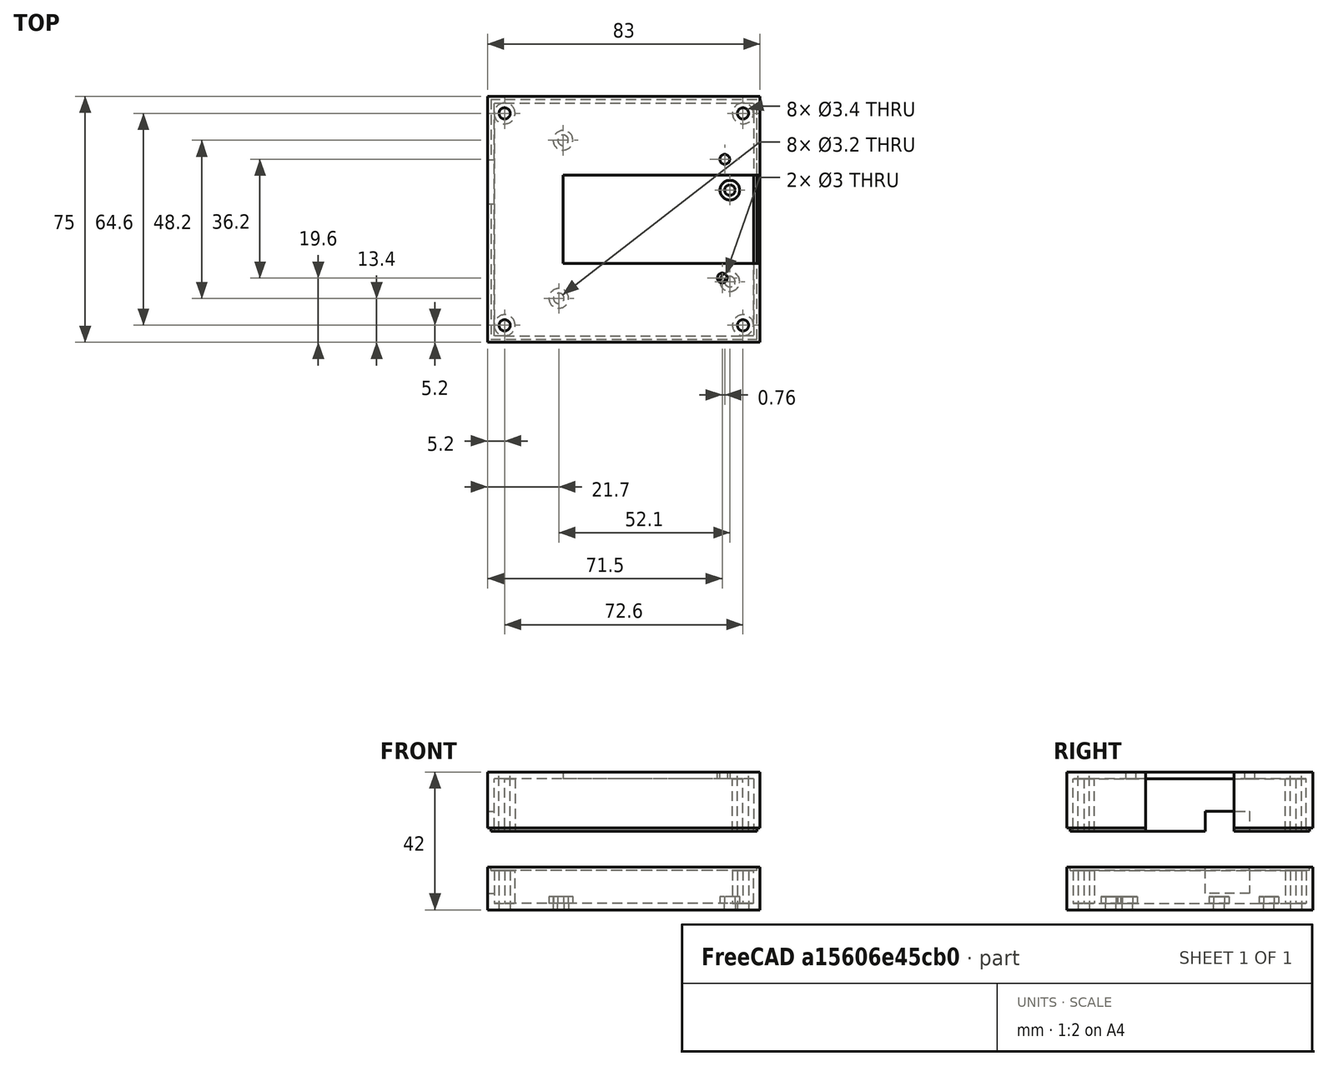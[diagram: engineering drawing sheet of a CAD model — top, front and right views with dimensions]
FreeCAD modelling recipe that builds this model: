
FCSTD DOCUMENT  (FreeCAD 0.19R23578 (Git))
Label: fond
License: All rights reserved
LicenseURL: http://en.wikipedia.org/wiki/All_rights_reserved
objects: Sketcher::SketchObject×15, PartDesign::Pad×9, PartDesign::Pocket×4, PartDesign::Hole×2, PartDesign::Body×2
note: 47 computed .brp shape members not serialized (recipe doc carries the construction recipe); baked Part::Feature solids carry a one-line shape summary decoded from their .brp

FEATURE [Sketcher::SketchObject] Sketch
  MapMode = 5
  Support = -> [XY_Plane]
  sketch-geometry (4):
    g0: LineSegment StartX=-41.5 StartY=37.5 StartZ=0 EndX=41.5 EndY=37.5 EndZ=0
    g1: LineSegment StartX=41.5 StartY=37.5 StartZ=0 EndX=41.5 EndY=-37.5 EndZ=0
    g2: LineSegment StartX=41.5 StartY=-37.5 StartZ=0 EndX=-41.5 EndY=-37.5 EndZ=0
    g3: LineSegment StartX=-41.5 StartY=-37.5 StartZ=0 EndX=-41.5 EndY=37.5 EndZ=0
  constraints (10):
    c: Coincident(g0,g1)
    c: Coincident(g1,g2)
    c: Coincident(g2,g3)
    c: Coincident(g3,g0)
    c: Horizontal(g2)
    c: Vertical(g1)
    c: DistanceX(g0,g0) = 83
    c: DistanceY(g3,g3) = 75
    c: Symmetric(g0,g0,g-2)
    c: Symmetric(g2,g0,g-1)
FEATURE [PartDesign::Pad] Pad  label="PlaqueFond"
  Direction = (1,1,1)
  Length = 2
  Length2 = 100
  Profile = -> Sketch
  Type = 0
FEATURE [Sketcher::SketchObject] Sketch001
  ExternalGeometry = -> [Pad]
  MapMode = 5
  Placement = pos=(0,0,2) rot=(0,0,1;0rad)
  Support = -> [Pad]
  sketch-geometry (9):
    g0: Circle CenterX=-18.5 CenterY=24.1 CenterZ=0 NormalX=0 NormalY=0 NormalZ=1 AngleXU=0 Radius=1.6
    g1: Circle CenterX=32.3 CenterY=8.9 CenterZ=0 NormalX=0 NormalY=0 NormalZ=1 AngleXU=0 Radius=1.6
    g2: Circle CenterX=32.3 CenterY=-19 CenterZ=0 NormalX=0 NormalY=0 NormalZ=1 AngleXU=0 Radius=1.6
    g3: Circle CenterX=-19.8 CenterY=-24.1 CenterZ=0 NormalX=0 NormalY=0 NormalZ=1 AngleXU=0 Radius=1.6
    g4: Circle CenterX=-19.8 CenterY=-24.1 CenterZ=0 NormalX=0 NormalY=0 NormalZ=1 AngleXU=0 Radius=3
    g5: Circle CenterX=32.3 CenterY=-19 CenterZ=0 NormalX=0 NormalY=0 NormalZ=1 AngleXU=0 Radius=3
    g6: Circle CenterX=32.3 CenterY=8.9 CenterZ=0 NormalX=0 NormalY=0 NormalZ=1 AngleXU=0 Radius=3
    g7: Circle CenterX=-18.5 CenterY=24.1 CenterZ=0 NormalX=0 NormalY=0 NormalZ=1 AngleXU=0 Radius=3
    g8: LineSegment StartX=-18.5 StartY=24.1 StartZ=0 EndX=-19.8 EndY=24.1 EndZ=0
  constraints (22):
    c: Vertical(g2,g1)
    c: DistanceY(g3,g2) = 5.1
    c: DistanceY(g2,g1) = 27.9
    c: DistanceY(g1,g0) = 15.2
    c: DistanceX(g3,g0) = 1.3
    c: DistanceX(g0,g1) = 50.8
    c: Radius(g3) = 1.6
    c: Equal(g3,g2)
    c: Equal(g3,g1)
    c: Equal(g3,g0)
    c: Coincident(g7,g0)
    c: Coincident(g4,g3)
    c: Coincident(g5,g2)
    c: Coincident(g6,g1)
    c: Radius(g5) = 3
    c: Equal(g5,g6)
    c: Equal(g5,g4)
    c: Equal(g5,g7)
    c: Coincident(g8,g0)
    c: Horizontal(g8)
    c: Symmetric(g8,g3,g-1)
    c: DistanceX(g-3,g0) = 23
FEATURE [PartDesign::Pad] Pad001  label="FixationArduino"
  BaseFeature = -> Pad
  Direction = (1,1,1)
  Length = 2
  Length2 = 100
  Profile = -> Sketch001
  Type = 0
FEATURE [Sketcher::SketchObject] Sketch002
  ExternalGeometry = -> [Pad001]
  MapMode = 5
  Placement = pos=(0,0,2) rot=(0,0,1;0rad)
  Support = -> [Pad001]
  sketch-geometry (8):
    g0: LineSegment StartX=-41.5 StartY=37.5 StartZ=0 EndX=41.5 EndY=37.5 EndZ=0
    g1: LineSegment StartX=41.5 StartY=37.5 StartZ=0 EndX=41.5 EndY=-37.5 EndZ=0
    g2: LineSegment StartX=41.5 StartY=-37.5 StartZ=0 EndX=-41.5 EndY=-37.5 EndZ=0
    g3: LineSegment StartX=-41.5 StartY=-37.5 StartZ=0 EndX=-41.5 EndY=37.5 EndZ=0
    g4: LineSegment StartX=-39.5 StartY=35.5 StartZ=0 EndX=39.5 EndY=35.5 EndZ=0
    g5: LineSegment StartX=39.5 StartY=35.5 StartZ=0 EndX=39.5 EndY=-35.5 EndZ=0
    g6: LineSegment StartX=39.5 StartY=-35.5 StartZ=0 EndX=-39.5 EndY=-35.5 EndZ=0
    g7: LineSegment StartX=-39.5 StartY=-35.5 StartZ=0 EndX=-39.5 EndY=35.5 EndZ=0
  constraints (20):
    c: Coincident(g0,g1)
    c: Coincident(g1,g2)
    c: Coincident(g2,g3)
    c: Coincident(g3,g0)
    c: Horizontal(g0)
    c: Horizontal(g2)
    c: Vertical(g1)
    c: Vertical(g3)
    c: Coincident(g4,g5)
    c: Coincident(g5,g6)
    c: Coincident(g6,g7)
    c: Coincident(g7,g4)
    c: Horizontal(g6)
    c: Vertical(g5)
    c: Coincident(g0,g-4)
    c: Coincident(g2,g-6)
    c: Symmetric(g4,g4,g-2)
    c: Symmetric(g6,g4,g-1)
    c: DistanceX(g0,g4) = 2
    c: DistanceY(g4,g0) = 2
FEATURE [PartDesign::Pad] Pad002  label="Rebord"
  BaseFeature = -> Pad001
  Direction = (1,1,1)
  Length = 10
  Length2 = 100
  Profile = -> Sketch002
  Type = 0
FEATURE [Sketcher::SketchObject] Sketch003
  ExternalGeometry = -> [Pad002]
  MapMode = 5
  Placement = pos=(-41.5,0,0) rot=(0.57735,-0.57735,-0.57735;2.0944rad)
  Support = -> [Pad002]
  sketch-geometry (4):
    g0: LineSegment StartX=-18.21 StartY=5 StartZ=0 EndX=-4.71 EndY=5 EndZ=0
    g1: LineSegment StartX=-4.71 StartY=5 StartZ=0 EndX=-4.71 EndY=12 EndZ=0
    g2: LineSegment StartX=-4.71 StartY=12 StartZ=0 EndX=-18.21 EndY=12 EndZ=0
    g3: LineSegment StartX=-18.21 StartY=12 StartZ=0 EndX=-18.21 EndY=5 EndZ=0
  constraints (12):
    c: Coincident(g0,g1)
    c: Coincident(g1,g2)
    c: Coincident(g2,g3)
    c: Coincident(g3,g0)
    c: Horizontal(g0)
    c: Horizontal(g2)
    c: Vertical(g1)
    c: Vertical(g3)
    c: PointOnObject(g2,g-3)
    c: DistanceX(g0,g0) = 13.5
    c: DistanceY(g-4,g0) = 3
    c: DistanceX(g1,g-1) = 4.71
FEATURE [PartDesign::Pocket] Pocket  label="OuvertureUSB"
  BaseFeature = -> Pad002
  Length = 0
  Length2 = 100
  Profile = -> Sketch003
  Type = 2
FEATURE [Sketcher::SketchObject] Sketch004
  ExternalGeometry = -> [Pocket]
  MapMode = 5
  Placement = pos=(0,0,2) rot=(0,0,1;0rad)
  Support = -> [Pocket]
  sketch-geometry (4):
    g0: Circle CenterX=32.3 CenterY=8.9 CenterZ=0 NormalX=0 NormalY=0 NormalZ=1 AngleXU=0 Radius=1.6
    g1: Circle CenterX=32.3 CenterY=-19 CenterZ=0 NormalX=0 NormalY=0 NormalZ=1 AngleXU=0 Radius=1.6
    g2: Circle CenterX=-19.8 CenterY=-24.1 CenterZ=0 NormalX=0 NormalY=0 NormalZ=1 AngleXU=0 Radius=1.6
    g3: Circle CenterX=-18.5 CenterY=24.1 CenterZ=0 NormalX=0 NormalY=0 NormalZ=1 AngleXU=0 Radius=1.6
  constraints (8):
    c: Coincident(g3,g-6)
    c: Coincident(g0,g-3)
    c: Coincident(g1,g-4)
    c: Coincident(g2,g-5)
    c: Radius(g2) = 1.6
    c: Equal(g2,g1)
    c: Equal(g2,g0)
    c: Equal(g2,g3)
FEATURE [PartDesign::Pocket] Pocket001  label="TrouFixationArduino"
  BaseFeature = -> Pocket
  Length = 5
  Length2 = 100
  Profile = -> Sketch004
  Type = 2
FEATURE [Sketcher::SketchObject] Sketch005
  ExternalGeometry = -> [Pocket001]
  MapMode = 5
  Placement = pos=(0,0,12) rot=(0,0,1;0rad)
  Support = -> [Pocket001]
  sketch-geometry (12):
    g0: LineSegment StartX=41.5 StartY=37.5 StartZ=0 EndX=-41.5 EndY=37.5 EndZ=0
    g1: LineSegment StartX=41.5 StartY=-37.5 StartZ=0 EndX=41.5 EndY=37.5 EndZ=0
    g2: LineSegment StartX=41.5 StartY=-37.5 StartZ=0 EndX=-41.5 EndY=-37.5 EndZ=0
    g3: LineSegment StartX=-40.5 StartY=-36.5 StartZ=0 EndX=-40.5 EndY=4.71 EndZ=0
    g4: LineSegment StartX=-40.5 StartY=4.71 StartZ=0 EndX=-41.5 EndY=4.71 EndZ=0
    g5: LineSegment StartX=-41.5 StartY=4.71 StartZ=0 EndX=-41.5 EndY=-37.5 EndZ=0
    g6: LineSegment StartX=-40.5 StartY=36.5 StartZ=0 EndX=-40.5 EndY=18.21 EndZ=0
    g7: LineSegment StartX=-40.5 StartY=18.21 StartZ=0 EndX=-41.5 EndY=18.21 EndZ=0
    g8: LineSegment StartX=-41.5 StartY=18.21 StartZ=0 EndX=-41.5 EndY=37.5 EndZ=0
    g9: LineSegment StartX=40.5 StartY=36.5 StartZ=0 EndX=-40.5 EndY=36.5 EndZ=0
    g10: LineSegment StartX=40.5 StartY=-36.5 StartZ=0 EndX=40.5 EndY=36.5 EndZ=0
    g11: LineSegment StartX=-40.5 StartY=-36.5 StartZ=0 EndX=40.5 EndY=-36.5 EndZ=0
  constraints (30):
    c: Coincident(g3,g4)
    c: Coincident(g4,g5)
    c: Horizontal(g4)
    c: Vertical(g3)
    c: Coincident(g6,g7)
    c: Coincident(g7,g8)
    c: Horizontal(g7)
    c: Vertical(g6)
    c: Coincident(g2,g-12)
    c: Coincident(g4,g-10)
    c: Coincident(g7,g-8)
    c: DistanceX(g7,g7) = 1
    c: DistanceX(g4,g4) = 1
    c: Horizontal(g9)
    c: Coincident(g10,g9)
    c: Vertical(g10)
    c: Coincident(g11,g3)
    c: Coincident(g11,g10)
    c: Horizontal(g11)
    c: Coincident(g5,g2)
    c: DistanceY(g2,g3) = 1
    c: Coincident(g2,g1)
    c: Coincident(g1,g-12)
    c: DistanceX(g10,g1) = 1
    c: Coincident(g1,g0)
    c: DistanceY(g9,g0) = 1
    c: Coincident(g8,g0)
    c: Coincident(g6,g9)
    c: Coincident(g0,g-6)
    c: Coincident(g0,g-8)
FEATURE [PartDesign::Pad] Pad003  label="EncocheRebord"
  BaseFeature = -> Pocket001
  Direction = (1,1,1)
  Length = 1
  Length2 = 100
  Profile = -> Sketch005
  Type = 0
FEATURE [Sketcher::SketchObject] Sketch006
  ExternalGeometry = -> [Pad003]
  MapMode = 5
  Placement = pos=(0,0,2) rot=(0,0,1;0rad)
  Support = -> [Pad003]
  sketch-geometry (4):
    g0: Circle CenterX=-36.3 CenterY=32.3 CenterZ=0 NormalX=0 NormalY=0 NormalZ=1 AngleXU=0 Radius=3.2
    g1: Circle CenterX=36.3 CenterY=32.3 CenterZ=0 NormalX=0 NormalY=0 NormalZ=1 AngleXU=0 Radius=3.2
    g2: Circle CenterX=36.3 CenterY=-32.3 CenterZ=0 NormalX=0 NormalY=0 NormalZ=1 AngleXU=0 Radius=3.2
    g3: Circle CenterX=-36.3 CenterY=-32.3 CenterZ=0 NormalX=0 NormalY=0 NormalZ=1 AngleXU=0 Radius=3.2
  constraints (9):
    c: Symmetric(g3,g0,g-1)
    c: Symmetric(g2,g1,g-1)
    c: Symmetric(g1,g0,g-2)
    c: Radius(g1) = 3.2
    c: Equal(g1,g2)
    c: Equal(g1,g3)
    c: Equal(g1,g0)
    c: DistanceY(g0,g-4) = 3.2
    c: DistanceX(g-4,g0) = 3.2
FEATURE [PartDesign::Pad] Pad004  label="CylindreAssemblage"
  BaseFeature = -> Pad003
  Direction = (1,1,1)
  Length = 10
  Length2 = 100
  Profile = -> Sketch006
  Type = 0
FEATURE [Sketcher::SketchObject] Sketch007
  ExternalGeometry = -> [Pad004]
  MapMode = 5
  Placement = pos=(0,0,12) rot=(0,0,1;0rad)
  Support = -> [Pad004]
  sketch-geometry (4):
    g0: Circle CenterX=-36.3 CenterY=32.3 CenterZ=0 NormalX=0 NormalY=0 NormalZ=1 AngleXU=0 Radius=1
    g1: Circle CenterX=36.3 CenterY=32.3 CenterZ=0 NormalX=0 NormalY=0 NormalZ=1 AngleXU=0 Radius=1
    g2: Circle CenterX=36.3 CenterY=-32.3 CenterZ=0 NormalX=0 NormalY=0 NormalZ=1 AngleXU=0 Radius=1
    g3: Circle CenterX=-36.3 CenterY=-32.3 CenterZ=0 NormalX=0 NormalY=0 NormalZ=1 AngleXU=0 Radius=1
  constraints (8):
    c: Coincident(g0,g-3)
    c: Symmetric(g1,g0,g-2)
    c: Symmetric(g1,g2,g-1)
    c: Symmetric(g3,g2,g-2)
    c: Radius(g2) = 1
    c: Equal(g2,g3)
    c: Equal(g2,g0)
    c: Equal(g2,g1)
FEATURE [PartDesign::Hole] Hole  label="TrouCylindreAssemblage"
  BaseFeature = -> Pad004
  Depth = 25
  DepthType = 0
  Diameter = 3.4
  DrillPoint = 1
  DrillPointAngle = 118
  HoleCutCountersinkAngle = 90
  HoleCutDepth = 0
  HoleCutDiameter = 0
  HoleCutType = 0
  ModelActualThread = false
  Profile = -> Sketch007
  Tapered = false
  TaperedAngle = 90
  ThreadAngle = 0
  ThreadClass = 0
  ThreadCutOffInner = 0
  ThreadCutOffOuter = 0
  ThreadDirection = 0
  ThreadFit = 0
  ThreadPitch = 0
  ThreadSize = 9
  ThreadType = 1
  Threaded = false
FEATURE [PartDesign::Body] Body  label="Fond"
  Group = -> [Sketch,Pad,Sketch001,Pad001,Sketch002,Pad002,Sketch003,Pocket,Sketch004,Pocket001,Sketch005,Pad003,Sketch006,Pad004,Sketch007,Hole]
  Origin = -> Origin
  Tip = -> Hole
FEATURE [Sketcher::SketchObject] Sketch008
  MapMode = 5
  Support = -> [XY_Plane001]
  sketch-geometry (4):
    g0: LineSegment StartX=-41.5 StartY=37.5 StartZ=0 EndX=41.5 EndY=37.5 EndZ=0
    g1: LineSegment StartX=41.5 StartY=37.5 StartZ=0 EndX=41.5 EndY=-37.5 EndZ=0
    g2: LineSegment StartX=41.5 StartY=-37.5 StartZ=0 EndX=-41.5 EndY=-37.5 EndZ=0
    g3: LineSegment StartX=-41.5 StartY=-37.5 StartZ=0 EndX=-41.5 EndY=37.5 EndZ=0
  constraints (10):
    c: Coincident(g0,g1)
    c: Coincident(g1,g2)
    c: Coincident(g2,g3)
    c: Coincident(g3,g0)
    c: Horizontal(g2)
    c: Vertical(g1)
    c: Symmetric(g0,g0,g-2)
    c: Symmetric(g2,g0,g-1)
    c: DistanceX(g0,g0) = 83
    c: DistanceY(g3,g3) = 75
FEATURE [PartDesign::Pad] Pad005  label="PlaqueDessus"
  Direction = (1,1,1)
  Length = 2
  Length2 = 100
  Profile = -> Sketch008
  Type = 0
FEATURE [Sketcher::SketchObject] Sketch009
  ExternalGeometry = -> [Pad005]
  MapMode = 5
  Placement = pos=(0,0,0) rot=(1,0,0;3.14159rad)
  Support = -> [Pad005]
  sketch-geometry (8):
    g0: LineSegment StartX=-41.5 StartY=37.5 StartZ=0 EndX=41.5 EndY=37.5 EndZ=0
    g1: LineSegment StartX=41.5 StartY=37.5 StartZ=0 EndX=41.5 EndY=-37.5 EndZ=0
    g2: LineSegment StartX=41.5 StartY=-37.5 StartZ=0 EndX=-41.5 EndY=-37.5 EndZ=0
    g3: LineSegment StartX=-41.5 StartY=-37.5 StartZ=0 EndX=-41.5 EndY=37.5 EndZ=0
    g4: LineSegment StartX=-39.5 StartY=35.5 StartZ=0 EndX=39.5 EndY=35.5 EndZ=0
    g5: LineSegment StartX=39.5 StartY=35.5 StartZ=0 EndX=39.5 EndY=-35.5 EndZ=0
    g6: LineSegment StartX=39.5 StartY=-35.5 StartZ=0 EndX=-39.5 EndY=-35.5 EndZ=0
    g7: LineSegment StartX=-39.5 StartY=-35.5 StartZ=0 EndX=-39.5 EndY=35.5 EndZ=0
  constraints (22):
    c: Coincident(g0,g1)
    c: Coincident(g1,g2)
    c: Coincident(g2,g3)
    c: Coincident(g3,g0)
    c: Horizontal(g0)
    c: Horizontal(g2)
    c: Vertical(g1)
    c: Vertical(g3)
    c: Coincident(g4,g5)
    c: Coincident(g5,g6)
    c: Coincident(g6,g7)
    c: Coincident(g7,g4)
    c: Horizontal(g4)
    c: Horizontal(g6)
    c: Vertical(g5)
    c: Vertical(g7)
    c: Coincident(g0,g-4)
    c: Coincident(g2,g-6)
    c: DistanceY(g2,g6) = 2
    c: DistanceY(g4,g0) = 2
    c: DistanceX(g0,g4) = 2
    c: DistanceX(g4,g0) = 2
FEATURE [PartDesign::Pad] Pad006  label="RebordDessus"
  BaseFeature = -> Pad005
  Direction = (1,1,1)
  Length = 15
  Length2 = 100
  Profile = -> Sketch009
  Type = 0
FEATURE [Sketcher::SketchObject] Sketch010
  ExternalGeometry = -> [Pad006]
  MapMode = 5
  Placement = pos=(-41.5,0,0) rot=(0.57735,-0.57735,-0.57735;2.0944rad)
  Support = -> [Pad006]
  sketch-geometry (4):
    g0: LineSegment StartX=-18.21 StartY=-15 StartZ=0 EndX=-4.71 EndY=-15 EndZ=0
    g1: LineSegment StartX=-4.71 StartY=-15 StartZ=0 EndX=-4.71 EndY=-10 EndZ=0
    g2: LineSegment StartX=-4.71 StartY=-10 StartZ=0 EndX=-18.21 EndY=-10 EndZ=0
    g3: LineSegment StartX=-18.21 StartY=-10 StartZ=0 EndX=-18.21 EndY=-15 EndZ=0
  constraints (12):
    c: Coincident(g0,g1)
    c: Coincident(g1,g2)
    c: Coincident(g2,g3)
    c: Coincident(g3,g0)
    c: Horizontal(g0)
    c: Horizontal(g2)
    c: Vertical(g1)
    c: Vertical(g3)
    c: DistanceY(g3,g3) = 5
    c: PointOnObject(g0,g-3)
    c: DistanceX(g1,g-1) = 4.71
    c: DistanceX(g2,g2) = 13.5
FEATURE [PartDesign::Pocket] Pocket002  label="DessusOuvertureUSB"
  BaseFeature = -> Pad006
  Length = 5
  Length2 = 100
  Profile = -> Sketch010
  Type = 2
FEATURE [Sketcher::SketchObject] Sketch011
  ExternalGeometry = -> [Pad006]
  MapMode = 5
  Placement = pos=(0,0,0) rot=(1,0,0;3.14159rad)
  Support = -> [Pad006]
  sketch-geometry (4):
    g0: Circle CenterX=36.3 CenterY=32.3 CenterZ=0 NormalX=0 NormalY=0 NormalZ=1 AngleXU=0 Radius=3.2
    g1: Circle CenterX=36.3 CenterY=-32.3 CenterZ=0 NormalX=0 NormalY=0 NormalZ=1 AngleXU=0 Radius=3.2
    g2: Circle CenterX=-36.3 CenterY=-32.3 CenterZ=0 NormalX=0 NormalY=0 NormalZ=1 AngleXU=0 Radius=3.2
    g3: Circle CenterX=-36.3 CenterY=32.3 CenterZ=0 NormalX=0 NormalY=0 NormalZ=1 AngleXU=0 Radius=3.2
  constraints (9):
    c: Symmetric(g3,g2,g-1)
    c: Symmetric(g1,g0,g-1)
    c: Symmetric(g3,g0,g-2)
    c: Radius(g3) = 3.2
    c: Equal(g3,g0)
    c: Equal(g3,g1)
    c: Equal(g3,g2)
    c: DistanceY(g0,g-4) = 3.2
    c: DistanceX(g0,g-4) = 3.2
FEATURE [PartDesign::Pad] Pad007  label="CylindreAssemblageDessus"
  BaseFeature = -> Pocket002
  Direction = (1,1,1)
  Length = 16
  Length2 = 100
  Profile = -> Sketch011
  Type = 0
FEATURE [Sketcher::SketchObject] Sketch012
  ExternalGeometry = -> [Pad007]
  MapMode = 5
  Placement = pos=(0,0,-16) rot=(1,0,0;3.14159rad)
  Support = -> [Pad007]
  sketch-geometry (4):
    g0: Circle CenterX=-36.3 CenterY=32.3 CenterZ=0 NormalX=0 NormalY=0 NormalZ=1 AngleXU=0 Radius=1
    g1: Circle CenterX=36.3 CenterY=32.3 CenterZ=0 NormalX=0 NormalY=0 NormalZ=1 AngleXU=0 Radius=1
    g2: Circle CenterX=36.3 CenterY=-32.3 CenterZ=0 NormalX=0 NormalY=0 NormalZ=1 AngleXU=0 Radius=1
    g3: Circle CenterX=-36.3 CenterY=-32.3 CenterZ=0 NormalX=0 NormalY=0 NormalZ=1 AngleXU=0 Radius=1
  constraints (8):
    c: Coincident(g0,g-6)
    c: Coincident(g1,g-3)
    c: Coincident(g2,g-4)
    c: Coincident(g3,g-5)
    c: Radius(g3) = 1
    c: Equal(g3,g2)
    c: Equal(g3,g1)
    c: Equal(g3,g0)
FEATURE [PartDesign::Hole] Hole001  label="TrouDessus"
  BaseFeature = -> Pad007
  Depth = 25
  DepthType = 1
  Diameter = 3.4
  DrillPoint = 1
  DrillPointAngle = 118
  HoleCutCountersinkAngle = 90
  HoleCutDepth = 0
  HoleCutDiameter = 0
  HoleCutType = 0
  ModelActualThread = false
  Profile = -> Sketch012
  Tapered = false
  TaperedAngle = 90
  ThreadAngle = 0
  ThreadClass = 0
  ThreadCutOffInner = 0
  ThreadCutOffOuter = 0
  ThreadDirection = 0
  ThreadFit = 0
  ThreadPitch = 0
  ThreadSize = 9
  ThreadType = 1
  Threaded = false
FEATURE [Sketcher::SketchObject] Sketch013
  ExternalGeometry = -> [Hole001]
  MapMode = 5
  Placement = pos=(0,0,-15) rot=(1,0,0;3.14159rad)
  Support = -> [Hole001]
  sketch-geometry (12):
    g0: LineSegment StartX=-39.5 StartY=-4.71 StartZ=0 EndX=-40.5 EndY=-4.71 EndZ=0
    g1: LineSegment StartX=-40.5 StartY=-4.71 StartZ=0 EndX=-40.5 EndY=36.5 EndZ=0
    g2: LineSegment StartX=-40.5 StartY=36.5 StartZ=0 EndX=40.5 EndY=36.5 EndZ=0
    g3: LineSegment StartX=40.5 StartY=36.5 StartZ=0 EndX=40.5 EndY=-36.5 EndZ=0
    g4: LineSegment StartX=40.5 StartY=-36.5 StartZ=0 EndX=-40.5 EndY=-36.5 EndZ=0
    g5: LineSegment StartX=-40.5 StartY=-36.5 StartZ=0 EndX=-40.5 EndY=-18.21 EndZ=0
    g6: LineSegment StartX=-40.5 StartY=-18.21 StartZ=0 EndX=-39.5 EndY=-18.21 EndZ=0
    g7: LineSegment StartX=-39.5 StartY=-18.21 StartZ=0 EndX=-39.5 EndY=-35.5 EndZ=0
    g8: LineSegment StartX=-39.5 StartY=-35.5 StartZ=0 EndX=39.5 EndY=-35.5 EndZ=0
    g9: LineSegment StartX=39.5 StartY=-35.5 StartZ=0 EndX=39.5 EndY=35.5 EndZ=0
    g10: LineSegment StartX=39.5 StartY=35.5 StartZ=0 EndX=-39.5 EndY=35.5 EndZ=0
    g11: LineSegment StartX=-39.5 StartY=35.5 StartZ=0 EndX=-39.5 EndY=-4.71 EndZ=0
  constraints (30):
    c: Coincident(g-6,g0)
    c: Horizontal(g0)
    c: Coincident(g0,g1)
    c: Vertical(g1)
    c: Coincident(g1,g2)
    c: Horizontal(g2)
    c: Coincident(g2,g3)
    c: Vertical(g3)
    c: Coincident(g3,g4)
    c: Horizontal(g4)
    c: Coincident(g4,g5)
    c: PointOnObject(g5,g-13)
    c: Vertical(g5)
    c: Coincident(g5,g6)
    c: Coincident(g6,g-13)
    c: Coincident(g6,g7)
    c: Coincident(g7,g-14)
    c: Coincident(g7,g8)
    c: Coincident(g8,g-15)
    c: Coincident(g8,g9)
    c: Coincident(g9,g-16)
    c: Coincident(g9,g10)
    c: Coincident(g10,g-17)
    c: Coincident(g10,g11)
    c: Coincident(g11,g0)
    c: DistanceX(g0,g0) = 1
    c: DistanceY(g10,g1) = 1
    c: DistanceX(g9,g2) = 1
    c: DistanceY(g3,g8) = 1
    c: DistanceX(g4,g7) = 1
FEATURE [PartDesign::Pad] Pad008  label="EncocheDessus"
  BaseFeature = -> Hole001
  Direction = (1,1,1)
  Length = 1
  Length2 = 100
  Profile = -> Sketch013
  Type = 0
FEATURE [Sketcher::SketchObject] Sketch014
  ExternalGeometry = -> [Pad008]
  MapMode = 5
  Placement = pos=(0,0,2) rot=(0,0,1;0rad)
  Support = -> [Pad008]
  sketch-geometry (6):
    g0: LineSegment StartX=-18.5 StartY=13.5 StartZ=0 EndX=41.5 EndY=13.5 EndZ=0
    g1: LineSegment StartX=41.5 StartY=13.5 StartZ=0 EndX=41.5 EndY=-13.5 EndZ=0
    g2: LineSegment StartX=41.5 StartY=-13.5 StartZ=0 EndX=-18.5 EndY=-13.5 EndZ=0
    g3: LineSegment StartX=-18.5 StartY=-13.5 StartZ=0 EndX=-18.5 EndY=13.5 EndZ=0
    g4: Circle CenterX=30.76 CenterY=18.3 CenterZ=0 NormalX=0 NormalY=0 NormalZ=1 AngleXU=0 Radius=1.5
    g5: Circle CenterX=30 CenterY=-17.9 CenterZ=0 NormalX=0 NormalY=0 NormalZ=1 AngleXU=0 Radius=1.5
  constraints (17):
    c: Coincident(g0,g1)
    c: Coincident(g1,g2)
    c: Coincident(g2,g3)
    c: Coincident(g3,g0)
    c: Horizontal(g0)
    c: Horizontal(g2)
    c: Vertical(g1)
    c: PointOnObject(g1,g-3)
    c: Symmetric(g2,g0,g-1)
    c: DistanceY(g2,g0) = 27
    c: DistanceX(g2,g2) = 60
    c: Radius(g5) = 1.5
    c: Equal(g5,g4)
    c: DistanceY(g5,g4) = 36.2
    c: DistanceX(g5,g4) = 0.76
    c: DistanceY(g5,g-1) = 17.9
    c: DistanceX(g5,g-3) = 11.5
FEATURE [PartDesign::Pocket] Pocket003  label="TrouEEPROM"
  BaseFeature = -> Pad008
  Length = 0
  Length2 = 100
  Profile = -> Sketch014
  Type = 1
FEATURE [PartDesign::Body] Body001  label="Dessus"
  Group = -> [Sketch008,Pad005,Sketch009,Pad006,Sketch010,Pocket002,Sketch011,Pad007,Sketch012,Hole001,Sketch013,Pad008,Sketch014,Pocket003]
  Origin = -> Origin001
  Placement = pos=(0,0,40) rot=(0,0,1;0rad)
  Tip = -> Pocket003
